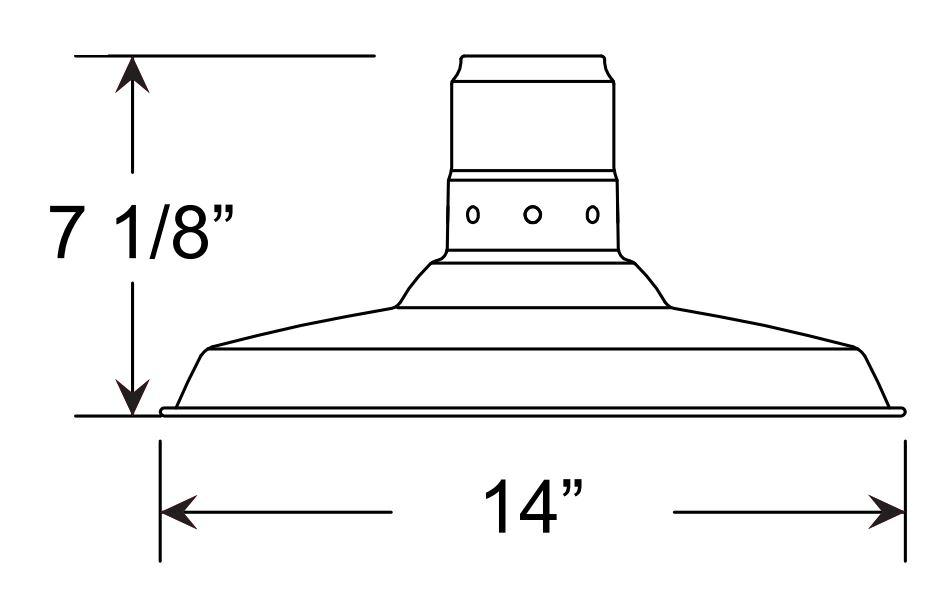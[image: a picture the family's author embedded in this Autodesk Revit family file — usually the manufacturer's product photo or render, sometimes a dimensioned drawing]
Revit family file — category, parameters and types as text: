
# Revit family: Emblem_MB
name_source: partatom
category: Lighting Fixtures
units: mm (PartAtom-declared; Revit-internal decimal feet)

## family parameters
Always vertical = Yes
Cut with Voids When Loaded = No
Light Source = Yes
OmniClass Number = 23.80.70.00
OmniClass Title = Lighting
Part Type = Normal
Room Calculation Point = No
Round Connector Dimension = Use Diameter
Shared = No
Work Plane-Based = No

## types (4) — shared parameters
Body Colour = Spun aluminium
Body Material = body
CRI = >90
Color Filter = 16777215
Construction Material = Heavy Duty spun aluminum.
Default Elevation = 0' - 0"
Description = 120-277 Voltage
Dimming = 1%
Dimming Lamp Color Temperature Shift = <None>
Efficiency = 65-125 lumens per watt
Inside body material = <By Category>
Life = L70 50,000 hours
Load Classification = Lighting
Manufacturer = ANP Lighting
Power Factor = 1
Tilt Angle = 90.00°
URL = https://www.anplighting.com
Voltage = 277 V
Warranty = 5 year limited warranty

## per-type parameters (varying)
| type | Apparent Load | Fixture Diameter | Fixture Height | Lamp | M707 | M710 | M712 | M714 | Photometric Web File | Wattage Comments | Weight |
| M707 | 100 VA | 0' - 7" | 0' - 6" | 100w Max Medium Base | Yes | No | No | No | M707M009LDNW40K.IES | 100W Max | 1.0 lb |
| M710 | 100 VA | 0' - 10" | 0' - 8" | 100w Max Medium Base | No | Yes | No | No | M707M009LDNW40K.IES | 100W | 1.0 lb |
| M712 | 200 VA | 1' - 0" | 0' - 9 1/2" | 200w Max Medium Base | No | No | Yes | No | M707M009LDNW40K.IES | 200W | 1.0 lb |
| M714 | 200 VA | 1' - 2" | 0' - 10" | 200w Max Medium Base | No | No | No | Yes | M714M016LDNW40K.ies | 200W | 1.5 lb |

note: column(s) folded — value = type name in every type: Model

## geometry (parser evidence)
native form markers: Sweep x26
no freeform markers — native parametric forms only
